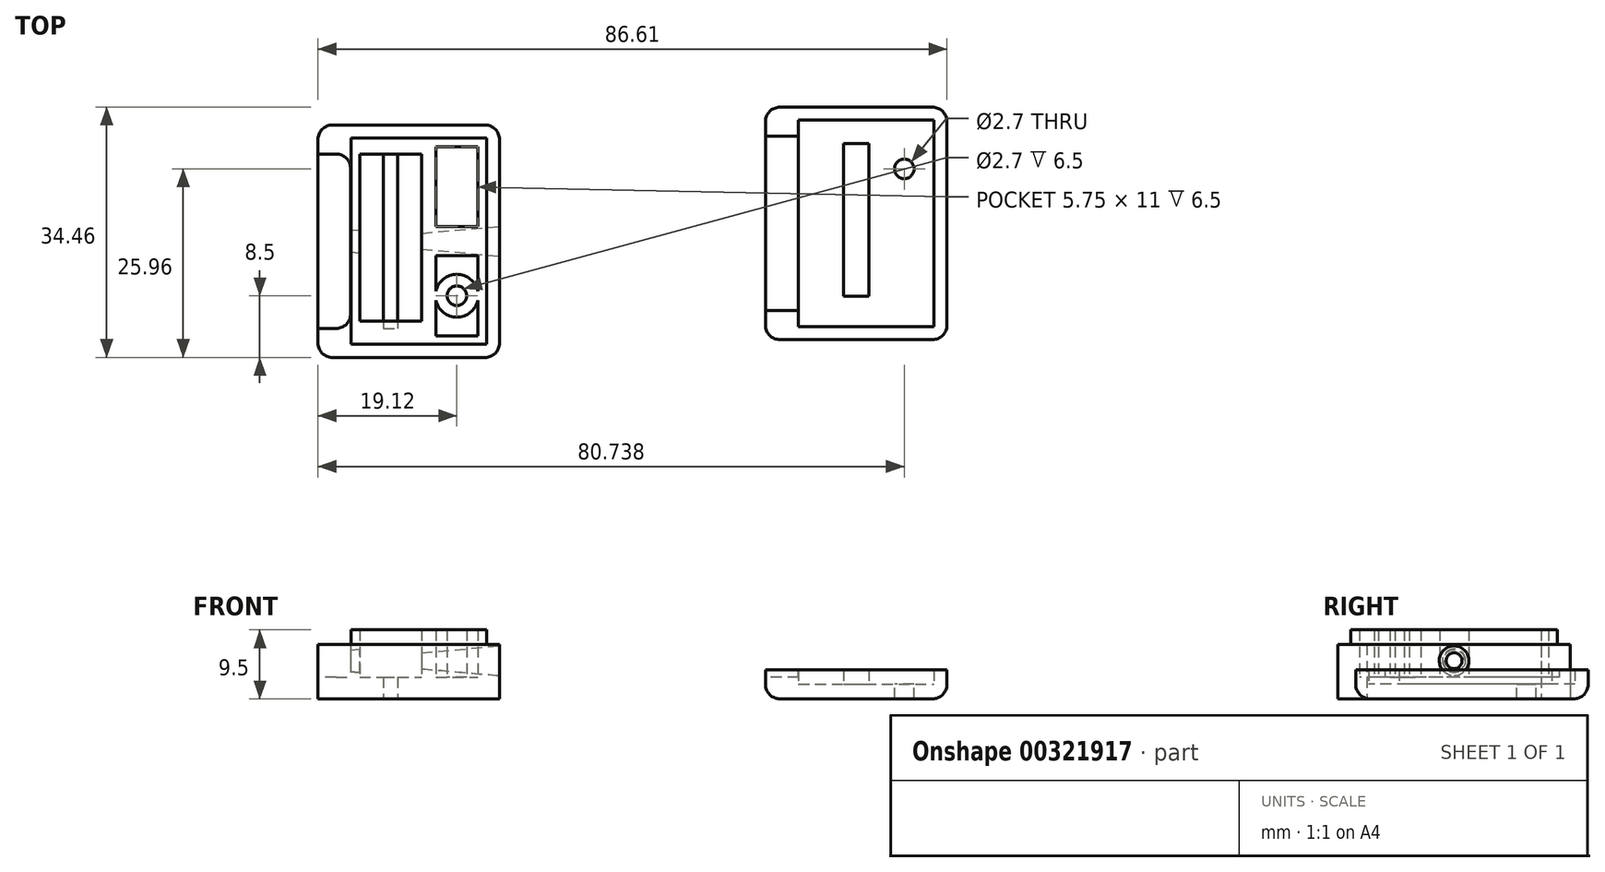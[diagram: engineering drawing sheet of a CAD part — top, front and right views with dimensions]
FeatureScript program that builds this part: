
annotation { "Feature Type Name" : "Feature", "Feature Type Description" : "" }
export const myFeature = defineFeature(function(context is Context, id is Id, definition is map)
    precondition{}
    {
        {
            var Q0;
            Q0=qCreatedBy(makeId("Top.planeOp"),FACE);
            var sketch = newSketch(context, id + "F0", { "sketchPlane" : qUnion([Q0])});
            skLineSegment(sketch, "E0.bottom", {"start": v(-40.4, 29.54) * mm, "end": v(-15.4, 29.54) * mm});
            skLineSegment(sketch, "E0.top", {"start": v(-40.4, -2.46) * mm, "end": v(-15.4, -2.46) * mm});
            skLineSegment(sketch, "E0.left", {"start": v(-40.4, 29.54) * mm, "end": v(-40.4, -2.46) * mm});
            skLineSegment(sketch, "E0.right", {"start": v(-15.4, 29.54) * mm, "end": v(-15.4, -2.46) * mm});
            skLineSegment(sketch, "E1.bottom", {"start": v(-37.9, -2.46) * mm, "end": v(-17.9, -2.46) * mm});
            skLineSegment(sketch, "E1.top", {"start": v(-37.9, -27.46) * mm, "end": v(-17.9, -27.46) * mm});
            skLineSegment(sketch, "E1.left", {"start": v(-37.9, -2.46) * mm, "end": v(-37.9, -27.46) * mm});
            skLineSegment(sketch, "E1.right", {"start": v(-17.9, -2.46) * mm, "end": v(-17.9, -27.46) * mm});
            skLineSegment(sketch, "E2.bottom", {"start": v(-31.4, 25.54) * mm, "end": v(-29.4, 25.54) * mm});
            skLineSegment(sketch, "E2.top", {"start": v(-31.4, 1.54) * mm, "end": v(-29.4, 1.54) * mm});
            skLineSegment(sketch, "E2.left", {"start": v(-31.4, 25.54) * mm, "end": v(-31.4, 1.54) * mm});
            skLineSegment(sketch, "E2.right", {"start": v(-29.4, 25.54) * mm, "end": v(-29.4, 1.54) * mm});
            skSolve(sketch);
        }
        {
            var Q0;
            Q0=makeQuery(id+"F0.imprint","IMPRINT",FACE,{"disambiguationData":[TD([[makeQuery(id+"F0.imprint","IMPRINT",EDGE,{"derivedFrom":sQuery(id+"F0.wireOp",EDGE,"E0.bottom")}),-1.0]])]});
            var Q1;
            Q1=makeQuery(id+"F0.imprint","IMPRINT",FACE,{"disambiguationData":[TD([[makeQuery(id+"F0.imprint","IMPRINT",EDGE,{"derivedFrom":sQuery(id+"F0.wireOp",EDGE,"E1.bottom")}),-1.0]])]});
            extrude(context, id + "F1", {"entities" : qUnion([Q0, Q1]), "depth" : 3 * mm, "offsetDistance" : 25 * mm});
        }
        {
            var Q0;
            Q0=makeQuery(id+"F1.opExtrude","CAP_FACE",FACE,{"disambiguationData":[OSD([sQuery(id+"F0.wireOp",EDGE,"E0.bottom"),sQuery(id+"F0.wireOp",EDGE,"E0.top"),sQuery(id+"F0.wireOp",EDGE,"E0.left"),sQuery(id+"F0.wireOp",EDGE,"E0.right"),sQuery(id+"F0.wireOp",EDGE,"E1.top"),sQuery(id+"F0.wireOp",EDGE,"E1.left"),sQuery(id+"F0.wireOp",EDGE,"E1.right"),sQuery(id+"F0.wireOp",EDGE,"E2.bottom"),sQuery(id+"F0.wireOp",EDGE,"E2.top"),sQuery(id+"F0.wireOp",EDGE,"E2.left"),sQuery(id+"F0.wireOp",EDGE,"E2.right")])],"isStart":false});
            var sketch = newSketch(context, id + "F2", { "sketchPlane" : qUnion([Q0])});
            skCircle(sketch, "E3", {"center": v(-27.9, -17.46) * mm, "radius": 2.1 * mm});
            skPoint(sketch, "E3.centerSnap0", {"position": v(-27.9, -27.46) * mm});
            skLineSegment(sketch, "E4.right", {"start": v(-18.4, 26.54) * mm, "end": v(-18.4, 6.7) * mm});
            skLineSegment(sketch, "E5", {"start": v(-37.9, -2.46) * mm, "end": v(-17.9, -2.46) * mm});
            skLineSegment(sketch, "E6", {"start": v(-34.64, 26.54) * mm, "end": v(-34.64, 0.54) * mm});
            skLineSegment(sketch, "E7", {"start": v(-26.14, 26.54) * mm, "end": v(-26.14, 0.54) * mm});
            skLineSegment(sketch, "E8", {"start": v(-36.64, 26.54) * mm, "end": v(-36.64, 21.7) * mm});
            skLineSegment(sketch, "E9", {"start": v(-24.14, 26.54) * mm, "end": v(-24.14, 6.7) * mm});
            skLineSegment(sketch, "E10.trimOffspring", {"start": v(-34.64, 0.54) * mm, "end": v(-26.14, 0.54) * mm});
            skLineSegment(sketch, "E11.trimOffspring", {"start": v(-34.64, 26.54) * mm, "end": v(-26.14, 26.54) * mm});
            skLineSegment(sketch, "E12.trimOffspring", {"start": v(-24.14, 26.54) * mm, "end": v(-18.4, 26.54) * mm});
            skLineSegment(sketch, "E13.trimOffspring", {"start": v(-24.14, 0.54) * mm, "end": v(-18.4, 0.54) * mm});
            skLineSegment(sketch, "E14", {"start": v(-24.14, 15.54) * mm, "end": v(-18.4, 15.54) * mm});
            skLineSegment(sketch, "E15", {"start": v(-24.14, 11.54) * mm, "end": v(-18.4, 11.54) * mm});
            skArc(sketch, "E16", {"start": v(-24.14, 5.38) * mm, "mid": v(-21.27, 3.1) * mm, "end": v(-18.4, 5.38) * mm});
            skPoint(sketch, "E16.centerSnap0", {"position": v(-21.27, 0.54) * mm});
            skCircle(sketch, "E17", {"center": v(-21.27, 6.04) * mm, "radius": 1.35 * mm});
            skArc(sketch, "E18.trimOffspring", {"start": v(-18.4, 6.7) * mm, "mid": v(-21.27, 9) * mm, "end": v(-24.14, 6.7) * mm});
            skLineSegment(sketch, "E19.trimOffspring", {"start": v(-18.4, 5.38) * mm, "end": v(-18.4, 0.54) * mm});
            skLineSegment(sketch, "E20.trimOffspring", {"start": v(-24.14, 5.38) * mm, "end": v(-24.14, 0.54) * mm});
            skLineSegment(sketch, "E21.trimOffspring", {"start": v(-36.64, 20.38) * mm, "end": v(-36.64, 0.54) * mm});
            skLineSegment(sketch, "E22", {"start": v(-36.64, 20.38) * mm, "end": v(-36.64, 21.7) * mm});
            skSolve(sketch);
        }
        {
            var Q0;
            Q0=makeQuery(id+"F2.imprint","IMPRINT",FACE,{"disambiguationData":[TD([[makeQuery(id+"F2.imprint","IMPRINT",EDGE,{"derivedFrom":sQuery(id+"F2.wireOp",EDGE,"E4.bottom")}),1.0]])]});
            var Q1;
            {var subQ0=sQuery(id+"F2.wireOp",EDGE,"Gw8Dyl51-lzw3-6a7q-cuhN-po8gZeIl9JzI");Q1=makeQuery(id+"F2.imprint","IMPRINT",FACE,{"disambiguationData":[TD([[makeQuery(id+"F2.imprint","IMPRINT",EDGE,{"derivedFrom":subQ0}),-1.0]])]});}
            var Q2;
            {var subQ0=sQuery(id+"F2.wireOp",EDGE,"E14");Q2=makeQuery(id+"F2.imprint","IMPRINT",FACE,{"disambiguationData":[TD([[makeQuery(id+"F2.imprint","IMPRINT",EDGE,{"derivedFrom":subQ0}),-1.0]])]});}
            var Q3;
            Q3=makeQuery(id+"F2.imprint","IMPRINT",FACE,{"disambiguationData":[TD([[makeQuery(id+"F2.imprint","IMPRINT",EDGE,{"derivedFrom":sQuery(id+"F2.wireOp",EDGE,"CIBxX4JK-zY8y-FO4m-0MgV-1SXS5KquZZtz")}),-1.0]])]});
            var Q4;
            Q4=makeQuery(id+"F2.imprint","IMPRINT",FACE,{"disambiguationData":[TD([[makeQuery(id+"F2.imprint","IMPRINT",EDGE,{"derivedFrom":sQuery(id+"F2.wireOp",EDGE,"E17")}),-1.0]])]});
            extrude(context, id + "F3", {"entities" : qUnion([Q0, Q1, Q2, Q3, Q4]), "operationType" : NewBodyOperationType.ADD, "depth" : 4.5 * mm, "offsetDistance" : 25 * mm});
        }
        {
            var Q0;
            Q0=makeQuery(id+"F2.imprint","IMPRINT",FACE,{"disambiguationData":[TD([[makeQuery(id+"F2.imprint","IMPRINT",EDGE,{"derivedFrom":sQuery(id+"F2.wireOp",EDGE,"E3")}),1.0]])]});
            extrude(context, id + "F4", {"entities" : qUnion([Q0]), "operationType" : NewBodyOperationType.REMOVE, "oppositeDirection" : true, "depth" : 25 * mm, "offsetDistance" : 25 * mm});
        }
        {
            var Q0;
            Q0=makeQuery(id+"F3.opExtrude","CAP_FACE",FACE,{"disambiguationData":[OSD([sQuery(id+"F0.wireOp",EDGE,"E0.bottom"),sQuery(id+"F0.wireOp",EDGE,"E0.top"),sQuery(id+"F0.wireOp",EDGE,"E0.left"),sQuery(id+"F0.wireOp",EDGE,"E0.right"),sQuery(id+"F2.wireOp",EDGE,"E4.bottom"),sQuery(id+"F2.wireOp",EDGE,"E4.top"),sQuery(id+"F2.wireOp",EDGE,"E4.left"),sQuery(id+"F2.wireOp",EDGE,"E4.right"),sQuery(id+"F2.wireOp",EDGE,"E5"),sQuery(id+"F2.wireOp",EDGE,"E6"),sQuery(id+"F2.wireOp",EDGE,"E7"),sQuery(id+"F2.wireOp",EDGE,"E8"),sQuery(id+"F2.wireOp",EDGE,"E9"),sQuery(id+"F2.wireOp",EDGE,"E10.trimOffspring"),sQuery(id+"F2.wireOp",EDGE,"E11.trimOffspring"),sQuery(id+"F2.wireOp",EDGE,"E12.trimOffspring"),sQuery(id+"F2.wireOp",EDGE,"E13.trimOffspring")])],"isStart":false});
            var sketch = newSketch(context, id + "F5", { "sketchPlane" : qUnion([Q0])});
            skLineSegment(sketch, "E23.bottom", {"start": v(-35.84, 27.74) * mm, "end": v(-17.2, 27.74) * mm});
            skLineSegment(sketch, "E23.top", {"start": v(-35.84, -0.66) * mm, "end": v(-17.2, -0.66) * mm});
            skLineSegment(sketch, "E23.left", {"start": v(-35.84, 27.74) * mm, "end": v(-35.84, -0.66) * mm});
            skLineSegment(sketch, "E23.right", {"start": v(-17.2, 27.74) * mm, "end": v(-17.2, -0.66) * mm});
            skLineSegment(sketch, "E24", {"start": v(-26.14, 26.54) * mm, "end": v(-24.14, 26.54) * mm});
            skLineSegment(sketch, "E25", {"start": v(-26.14, 0.54) * mm, "end": v(-24.14, 0.54) * mm});
            skLineSegment(sketch, "E26", {"start": v(-18.4, 11.54) * mm, "end": v(-18.4, 15.54) * mm});
            skSolve(sketch);
        }
        {
            var Q0;
            Q0=makeQuery(id+"F5.imprint","IMPRINT",FACE,{"disambiguationData":[TD([[makeQuery(id+"F5.imprint","IMPRINT",EDGE,{"derivedFrom":sQuery(id+"F5.wireOp",EDGE,"E23.bottom")}),-1.0]])]});
            extrude(context, id + "F6", {"entities" : qUnion([Q0]), "operationType" : NewBodyOperationType.ADD, "depth" : 2 * mm, "offsetDistance" : 25 * mm});
        }
        {
            var Q0;
            {var subQ0=sQuery(id+"F2.wireOp",EDGE,"E7");Q0=makeQuery(id+"F6.boolean.opBoolean","MERGE",FACE,{"derivedFrom":[makeQuery(id+"F3.opExtrude","SWEPT_FACE",FACE,{"disambiguationData":[OSD([subQ0])]}),makeQuery(id+"F6.opExtrude","SWEPT_FACE",FACE,{"disambiguationData":[OSD([subQ0])]})]});}
            var sketch = newSketch(context, id + "F7", { "sketchPlane" : qUnion([Q0])});
            skCircle(sketch, "E27", {"center": v(-13.54, 5.25) * mm, "radius": 1.1 * mm});
            skPoint(sketch, "E27.centerSnap0", {"position": v(-26.54, 6.25) * mm});
            skPoint(sketch, "E27.centerSnap1", {"position": v(-13.54, 9.5) * mm});
            skSolve(sketch);
        }
        {
            var Q0;
            {var subQ0=sQuery(id+"F0.wireOp",EDGE,"E0.left");Q0=makeQuery(id+"F3.boolean.opBoolean","MERGE",FACE,{"derivedFrom":[makeQuery(id+"F1.opExtrude","SWEPT_FACE",FACE,{"disambiguationData":[OSD([subQ0])]}),makeQuery(id+"F3.opExtrude","SWEPT_FACE",FACE,{"disambiguationData":[OSD([subQ0])]})]});}
            var sketch = newSketch(context, id + "F8", { "sketchPlane" : qUnion([Q0])});
            skCircle(sketch, "E28", {"center": v(-13.54, 5.25) * mm, "radius": 1.1 * mm});
            skPoint(sketch, "E28.centerSnap0", {"position": v(-13.54, 7.5) * mm});
            skLineSegment(sketch, "E29.bottom", {"start": v(-25.54, 7.5) * mm, "end": v(-1.54, 7.5) * mm});
            skLineSegment(sketch, "E29.top", {"start": v(-25.54, 3) * mm, "end": v(-1.54, 3) * mm});
            skLineSegment(sketch, "E29.left", {"start": v(-25.54, 7.5) * mm, "end": v(-25.54, 3) * mm});
            skLineSegment(sketch, "E29.right", {"start": v(-1.54, 7.5) * mm, "end": v(-1.54, 3) * mm});
            skSolve(sketch);
        }
        {
            var Q0;
            Q0=makeQuery(id+"F8.imprint","IMPRINT",FACE,{"disambiguationData":[TD([[makeQuery(id+"F8.imprint","IMPRINT",EDGE,{"derivedFrom":sQuery(id+"F8.wireOp",EDGE,"E28")}),1.0]])]});
            var Q1;
            Q1=makeQuery(id+"F7.imprint","IMPRINT",FACE,{"disambiguationData":[TD([[makeQuery(id+"F7.imprint","IMPRINT",EDGE,{"derivedFrom":sQuery(id+"F7.wireOp",EDGE,"E27")}),1.0]])]});
            extrude(context, id + "F9", {"entities" : qUnion([Q0, Q1]), "operationType" : NewBodyOperationType.REMOVE, "oppositeDirection" : true, "depth" : 11 * mm, "offsetDistance" : 25 * mm, "hasDraft" : true, "draftAngle" : 5 * degree});
        }
        {
            var Q0;
            Q0=makeQuery(id+"F8.imprint","IMPRINT",FACE,{"disambiguationData":[TD([[makeQuery(id+"F8.imprint","IMPRINT",EDGE,{"derivedFrom":sQuery(id+"F8.wireOp",EDGE,"E28")}),-1.0]])]});
            extrude(context, id + "F10", {"entities" : qUnion([Q0]), "operationType" : NewBodyOperationType.REMOVE, "oppositeDirection" : true, "depth" : 4.5 * mm, "offsetDistance" : 25 * mm});
        }
        {
            var Q0;
            Q0=qCreatedBy(makeId("Top.planeOp"),FACE);
            var sketch = newSketch(context, id + "F11", { "sketchPlane" : qUnion([Q0])});
            skLineSegment(sketch, "E30.bottom", {"start": v(21.22, 32) * mm, "end": v(46.22, 32) * mm});
            skLineSegment(sketch, "E30.top", {"start": v(21.22, 0) * mm, "end": v(46.22, 0) * mm});
            skLineSegment(sketch, "E30.left", {"start": v(21.22, 32) * mm, "end": v(21.22, 0) * mm});
            skLineSegment(sketch, "E30.right", {"start": v(46.22, 32) * mm, "end": v(46.22, 0) * mm});
            skSolve(sketch);
        }
        {
            var Q0;
            Q0 = qSketchRegion(id + "F11", true);
            extrude(context, id + "F12", {"entities" : qUnion([Q0]), "depth" : 2 * mm, "offsetDistance" : 25 * mm});
        }
        {
            var Q0;
            Q0=makeQuery(id+"F12.opExtrude","CAP_FACE",FACE,{"disambiguationData":[OSD([sQuery(id+"F11.wireOp",EDGE,"E30.bottom"),sQuery(id+"F11.wireOp",EDGE,"E30.top"),sQuery(id+"F11.wireOp",EDGE,"E30.left"),sQuery(id+"F11.wireOp",EDGE,"E30.right")])],"isStart":false});
            var sketch = newSketch(context, id + "F13", { "sketchPlane" : qUnion([Q0])});
            skLineSegment(sketch, "E31.bottom", {"start": v(25.77, 30.2) * mm, "end": v(44.42, 30.2) * mm});
            skLineSegment(sketch, "E31.top", {"start": v(25.77, 1.8) * mm, "end": v(44.42, 1.8) * mm});
            skLineSegment(sketch, "E31.left", {"start": v(25.77, 30.2) * mm, "end": v(25.77, 1.8) * mm});
            skLineSegment(sketch, "E31.right", {"start": v(44.42, 30.2) * mm, "end": v(44.42, 1.8) * mm});
            skSolve(sketch);
        }
        {
            var Q0;
            Q0=makeQuery(id+"F13.imprint","IMPRINT",FACE,{"disambiguationData":[TD([[makeQuery(id+"F13.imprint","IMPRINT",EDGE,{"derivedFrom":sQuery(id+"F13.wireOp",EDGE,"E31.bottom")}),1.0]])]});
            extrude(context, id + "F14", {"entities" : qUnion([Q0]), "operationType" : NewBodyOperationType.ADD, "depth" : 2 * mm, "offsetDistance" : 25 * mm});
        }
        {
            var Q0;
            Q0=makeQuery(id+"F12.opExtrude","CAP_FACE",FACE,{"disambiguationData":[OSD([sQuery(id+"F11.wireOp",EDGE,"E30.bottom"),sQuery(id+"F11.wireOp",EDGE,"E30.top"),sQuery(id+"F11.wireOp",EDGE,"E30.left"),sQuery(id+"F11.wireOp",EDGE,"E30.right")])],"isStart":false});
            var sketch = newSketch(context, id + "F15", { "sketchPlane" : qUnion([Q0])});
            skLineSegment(sketch, "E32.bottom", {"start": v(31.97, 29) * mm, "end": v(35.47, 29) * mm});
            skLineSegment(sketch, "E32.top", {"start": v(31.97, 3) * mm, "end": v(35.47, 3) * mm});
            skLineSegment(sketch, "E32.left", {"start": v(31.97, 29) * mm, "end": v(31.97, 3) * mm});
            skLineSegment(sketch, "E32.right", {"start": v(35.47, 29) * mm, "end": v(35.47, 3) * mm});
            skCircle(sketch, "E33", {"center": v(40.35, 23.5) * mm, "radius": 1.35 * mm});
            skCircle(sketch, "E34", {"center": v(40.35, 23.5) * mm, "radius": 2.85 * mm});
            skSolve(sketch);
        }
        {
            var Q0;
            Q0=makeQuery(id+"F15.imprint","IMPRINT",FACE,{"disambiguationData":[TD([[makeQuery(id+"F15.imprint","IMPRINT",EDGE,{"derivedFrom":sQuery(id+"F15.wireOp",EDGE,"E32.bottom")}),-1.0]])]});
            extrude(context, id + "F16", {"entities" : qUnion([Q0]), "operationType" : NewBodyOperationType.ADD, "depth" : 2 * mm, "offsetDistance" : 25 * mm});
        }
        {
            var Q0;
            Q0=makeQuery(id+"F15.imprint","IMPRINT",FACE,{"disambiguationData":[TD([[makeQuery(id+"F15.imprint","IMPRINT",EDGE,{"derivedFrom":sQuery(id+"F15.wireOp",EDGE,"mHAnbMJy-GtJf-08AI-XceP-GagCGZu93Zec")}),1.0]])]});
            var Q1;
            Q1=makeQuery(id+"F15.imprint","IMPRINT",FACE,{"disambiguationData":[TD([[makeQuery(id+"F15.imprint","IMPRINT",EDGE,{"derivedFrom":sQuery(id+"F15.wireOp",EDGE,"E33")}),1.0]])]});
            extrude(context, id + "F17", {"entities" : qUnion([Q0, Q1]), "operationType" : NewBodyOperationType.REMOVE, "oppositeDirection" : true, "depth" : 25 * mm, "offsetDistance" : 25 * mm});
        }
        {
            var Q0;
            {var subQ0=sQuery(id+"F11.wireOp",EDGE,"E30.left");Q0=makeQuery(id+"F14.boolean.opBoolean","MERGE",FACE,{"derivedFrom":[makeQuery(id+"F12.opExtrude","SWEPT_FACE",FACE,{"disambiguationData":[OSD([subQ0])]}),makeQuery(id+"F14.opExtrude","SWEPT_FACE",FACE,{"disambiguationData":[OSD([subQ0])]})]});}
            var sketch = newSketch(context, id + "F18", { "sketchPlane" : qUnion([Q0])});
            skLineSegment(sketch, "E35.bottom", {"start": v(-28, 4) * mm, "end": v(-4, 4) * mm});
            skLineSegment(sketch, "E35.top", {"start": v(-28, 3) * mm, "end": v(-4, 3) * mm});
            skLineSegment(sketch, "E35.left", {"start": v(-28, 4) * mm, "end": v(-28, 3) * mm});
            skLineSegment(sketch, "E35.right", {"start": v(-4, 4) * mm, "end": v(-4, 3) * mm});
            skSolve(sketch);
        }
        {
            var Q0;
            Q0=makeQuery(id+"F18.imprint","IMPRINT",FACE,{"disambiguationData":[TD([[makeQuery(id+"F18.imprint","IMPRINT",EDGE,{"derivedFrom":sQuery(id+"F18.wireOp",EDGE,"E35.bottom")}),-1.0]])]});
            extrude(context, id + "F19", {"entities" : qUnion([Q0]), "operationType" : NewBodyOperationType.REMOVE, "oppositeDirection" : true, "depth" : 4.6 * mm, "offsetDistance" : 25 * mm});
        }
        {
            var Q0;
            {var subQ0=sQuery(id+"F0.wireOp",EDGE,"E0.left");var subQ1=sQuery(id+"F0.wireOp",EDGE,"E0.bottom");Q0=makeQuery(id+"F3.boolean.opBoolean","MERGE",EDGE,{"derivedFrom":[makeQuery(id+"F1.opExtrude","SWEPT_EDGE",EDGE,{"disambiguationData":[OSD([subQ1,subQ0])]}),makeQuery(id+"F3.opExtrude","SWEPT_EDGE",EDGE,{"disambiguationData":[OSD([subQ1,subQ0])]})]});}
            var Q1;
            {var subQ0=sQuery(id+"F0.wireOp",EDGE,"E0.left");var subQ1=sQuery(id+"F0.wireOp",EDGE,"E0.top");Q1=makeQuery(id+"F3.boolean.opBoolean","MERGE",EDGE,{"derivedFrom":[makeQuery(id+"F1.opExtrude","SWEPT_EDGE",EDGE,{"disambiguationData":[OSD([subQ1,subQ0])]}),makeQuery(id+"F3.opExtrude","SWEPT_EDGE",EDGE,{"disambiguationData":[OSD([subQ1,subQ0])]})]});}
            var Q2;
            Q2=makeQuery(id+"F10.boolean.opBoolean","COPY",EDGE,{"derivedFrom":makeQuery(id+"F10.opExtrude","CAP_EDGE",EDGE,{"disambiguationData":[OSD([sQuery(id+"F8.wireOp",EDGE,"E29.top")])],"isStart":true})});
            var Q3;
            Q3=makeQuery(id+"F10.boolean.opBoolean","COPY",EDGE,{"derivedFrom":makeQuery(id+"F10.opExtrude","CAP_EDGE",EDGE,{"disambiguationData":[OSD([sQuery(id+"F8.wireOp",EDGE,"E29.right")])],"isStart":true})});
            var Q4;
            {var subQ0=sQuery(id+"F0.wireOp",EDGE,"E0.right");var subQ1=sQuery(id+"F0.wireOp",EDGE,"E0.bottom");Q4=makeQuery(id+"F3.boolean.opBoolean","MERGE",EDGE,{"derivedFrom":[makeQuery(id+"F1.opExtrude","SWEPT_EDGE",EDGE,{"disambiguationData":[OSD([subQ1,subQ0])]}),makeQuery(id+"F3.opExtrude","SWEPT_EDGE",EDGE,{"disambiguationData":[OSD([subQ1,subQ0])]})]});}
            var Q5;
            {var subQ0=sQuery(id+"F0.wireOp",EDGE,"E0.right");var subQ1=sQuery(id+"F0.wireOp",EDGE,"E0.top");Q5=makeQuery(id+"F3.boolean.opBoolean","MERGE",EDGE,{"derivedFrom":[makeQuery(id+"F1.opExtrude","SWEPT_EDGE",EDGE,{"disambiguationData":[OSD([subQ1,subQ0])]}),makeQuery(id+"F3.opExtrude","SWEPT_EDGE",EDGE,{"disambiguationData":[OSD([subQ1,subQ0])]})]});}
            var Q6;
            Q6=makeQuery(id+"F3.opExtrude","CAP_EDGE",EDGE,{"disambiguationData":[OSD([sQuery(id+"F0.wireOp",EDGE,"E0.top"),sQuery(id+"F2.wireOp",EDGE,"E5")])],"isStart":true});
            var Q7;
            Q7=makeQuery(id+"F1.opExtrude","SWEPT_EDGE",EDGE,{"disambiguationData":[OSD([sQuery(id+"F0.wireOp",EDGE,"E1.top"),sQuery(id+"F0.wireOp",EDGE,"E1.right")])]});
            var Q8;
            Q8=makeQuery(id+"F1.opExtrude","SWEPT_EDGE",EDGE,{"disambiguationData":[OSD([sQuery(id+"F0.wireOp",EDGE,"E1.top"),sQuery(id+"F0.wireOp",EDGE,"E1.left")])]});
            var Q9;
            Q9=makeQuery(id+"F10.boolean.opBoolean","COPY",EDGE,{"derivedFrom":makeQuery(id+"F10.opExtrude","CAP_EDGE",EDGE,{"disambiguationData":[OSD([sQuery(id+"F8.wireOp",EDGE,"E29.left")])],"isStart":true})});
            var Q10;
            {var subQ0=sQuery(id+"F11.wireOp",EDGE,"E30.left");var subQ1=sQuery(id+"F11.wireOp",EDGE,"E30.top");Q10=makeQuery(id+"F14.boolean.opBoolean","MERGE",EDGE,{"derivedFrom":[makeQuery(id+"F12.opExtrude","SWEPT_EDGE",EDGE,{"disambiguationData":[OSD([subQ1,subQ0])]}),makeQuery(id+"F14.opExtrude","SWEPT_EDGE",EDGE,{"disambiguationData":[OSD([subQ1,subQ0])]})]});}
            var Q11;
            {var subQ0=sQuery(id+"F11.wireOp",EDGE,"E30.left");var subQ1=sQuery(id+"F11.wireOp",EDGE,"E30.bottom");Q11=makeQuery(id+"F14.boolean.opBoolean","MERGE",EDGE,{"derivedFrom":[makeQuery(id+"F12.opExtrude","SWEPT_EDGE",EDGE,{"disambiguationData":[OSD([subQ1,subQ0])]}),makeQuery(id+"F14.opExtrude","SWEPT_EDGE",EDGE,{"disambiguationData":[OSD([subQ1,subQ0])]})]});}
            var Q12;
            Q12=makeQuery(id+"F19.boolean.opBoolean","COPY",EDGE,{"derivedFrom":makeQuery(id+"F19.opExtrude","CAP_EDGE",EDGE,{"disambiguationData":[OSD([sQuery(id+"F18.wireOp",EDGE,"E35.left")])],"isStart":true})});
            var Q13;
            Q13=makeQuery(id+"F19.boolean.opBoolean","COPY",EDGE,{"derivedFrom":makeQuery(id+"F19.opExtrude","CAP_EDGE",EDGE,{"disambiguationData":[OSD([sQuery(id+"F18.wireOp",EDGE,"E35.right")])],"isStart":true})});
            var Q14;
            Q14=makeQuery(id+"F10.boolean.opBoolean","COPY",EDGE,{"derivedFrom":makeQuery(id+"F10.opExtrude","CAP_EDGE",EDGE,{"disambiguationData":[OSD([sQuery(id+"F8.wireOp",EDGE,"E29.right")])],"isStart":false})});
            var Q15;
            Q15=makeQuery(id+"F10.boolean.opBoolean","COPY",EDGE,{"derivedFrom":makeQuery(id+"F10.opExtrude","CAP_EDGE",EDGE,{"disambiguationData":[OSD([sQuery(id+"F8.wireOp",EDGE,"E29.left")])],"isStart":false})});
            var Q16;
            {var subQ0=sQuery(id+"F11.wireOp",EDGE,"E30.right");var subQ1=sQuery(id+"F11.wireOp",EDGE,"E30.top");Q16=makeQuery(id+"F14.boolean.opBoolean","MERGE",EDGE,{"derivedFrom":[makeQuery(id+"F12.opExtrude","SWEPT_EDGE",EDGE,{"disambiguationData":[OSD([subQ1,subQ0])]}),makeQuery(id+"F14.opExtrude","SWEPT_EDGE",EDGE,{"disambiguationData":[OSD([subQ1,subQ0])]})]});}
            var Q17;
            {var subQ0=sQuery(id+"F11.wireOp",EDGE,"E30.right");var subQ1=sQuery(id+"F11.wireOp",EDGE,"E30.bottom");Q17=makeQuery(id+"F14.boolean.opBoolean","MERGE",EDGE,{"derivedFrom":[makeQuery(id+"F12.opExtrude","SWEPT_EDGE",EDGE,{"disambiguationData":[OSD([subQ1,subQ0])]}),makeQuery(id+"F14.opExtrude","SWEPT_EDGE",EDGE,{"disambiguationData":[OSD([subQ1,subQ0])]})]});}
            var Q18;
            Q18=makeQuery(id+"F12.opExtrude","CAP_EDGE",EDGE,{"disambiguationData":[OSD([sQuery(id+"F11.wireOp",EDGE,"E30.bottom")])],"isStart":true});
            var Q19;
            Q19=makeQuery(id+"F12.opExtrude","CAP_EDGE",EDGE,{"disambiguationData":[OSD([sQuery(id+"F11.wireOp",EDGE,"E30.right")])],"isStart":true});
            var Q20;
            Q20=makeQuery(id+"F12.opExtrude","CAP_EDGE",EDGE,{"disambiguationData":[OSD([sQuery(id+"F11.wireOp",EDGE,"E30.top")])],"isStart":true});
            var Q21;
            Q21=makeQuery(id+"F12.opExtrude","CAP_EDGE",EDGE,{"disambiguationData":[OSD([sQuery(id+"F11.wireOp",EDGE,"E30.left")])],"isStart":true});
            fillet(context, id + "F20", {"entities" : qUnion([Q0, Q1, Q2, Q3, Q4, Q5, Q6, Q7, Q8, Q9, Q10, Q11, Q12, Q13, Q14, Q15, Q16, Q17, Q18, Q19, Q20, Q21]), "radius" : 2 * mm, "tangentPropagation" : true, "allowEdgeOverflow" : false});
        }
        {
            var Q0;
            {var subQ0=sQuery(id+"F2.wireOp",EDGE,"E10.trimOffspring");Q0=makeQuery(id+"F6.boolean.opBoolean","MERGE",FACE,{"derivedFrom":[makeQuery(id+"F3.opExtrude","SWEPT_FACE",FACE,{"disambiguationData":[OSD([subQ0])]}),makeQuery(id+"F6.opExtrude","SWEPT_FACE",FACE,{"disambiguationData":[OSD([subQ0])]})]});}
            extrude(context, id + "F21", {"entities" : qUnion([Q0]), "operationType" : NewBodyOperationType.ADD, "depth" : 2 * mm, "offsetDistance" : 25 * mm});
        }
        {
            var Q0;
            {var subQ0=sQuery(id+"F2.wireOp",EDGE,"E11.trimOffspring");Q0=makeQuery(id+"F6.boolean.opBoolean","MERGE",FACE,{"derivedFrom":[makeQuery(id+"F3.opExtrude","SWEPT_FACE",FACE,{"disambiguationData":[OSD([subQ0])]}),makeQuery(id+"F6.opExtrude","SWEPT_FACE",FACE,{"disambiguationData":[OSD([subQ0])]})]});}
            extrude(context, id + "F22", {"entities" : qUnion([Q0]), "operationType" : NewBodyOperationType.ADD, "depth" : 1 * mm, "offsetDistance" : 25 * mm});
        }
        {
            var Q0;
            Q0=makeQuery(id+"F16.opExtrude","SWEPT_FACE",FACE,{"disambiguationData":[OSD([sQuery(id+"F15.wireOp",EDGE,"E32.top")])]});
            extrude(context, id + "F23", {"entities" : qUnion([Q0]), "operationType" : NewBodyOperationType.REMOVE, "oppositeDirection" : true, "depth" : 3 * mm, "offsetDistance" : 25 * mm});
        }
        {
            var Q0;
            Q0=makeQuery(id+"F16.opExtrude","SWEPT_FACE",FACE,{"disambiguationData":[OSD([sQuery(id+"F15.wireOp",EDGE,"E32.bottom")])]});
            extrude(context, id + "F24", {"entities" : qUnion([Q0]), "operationType" : NewBodyOperationType.REMOVE, "oppositeDirection" : true, "depth" : 2 * mm, "offsetDistance" : 25 * mm});
        }
    });
